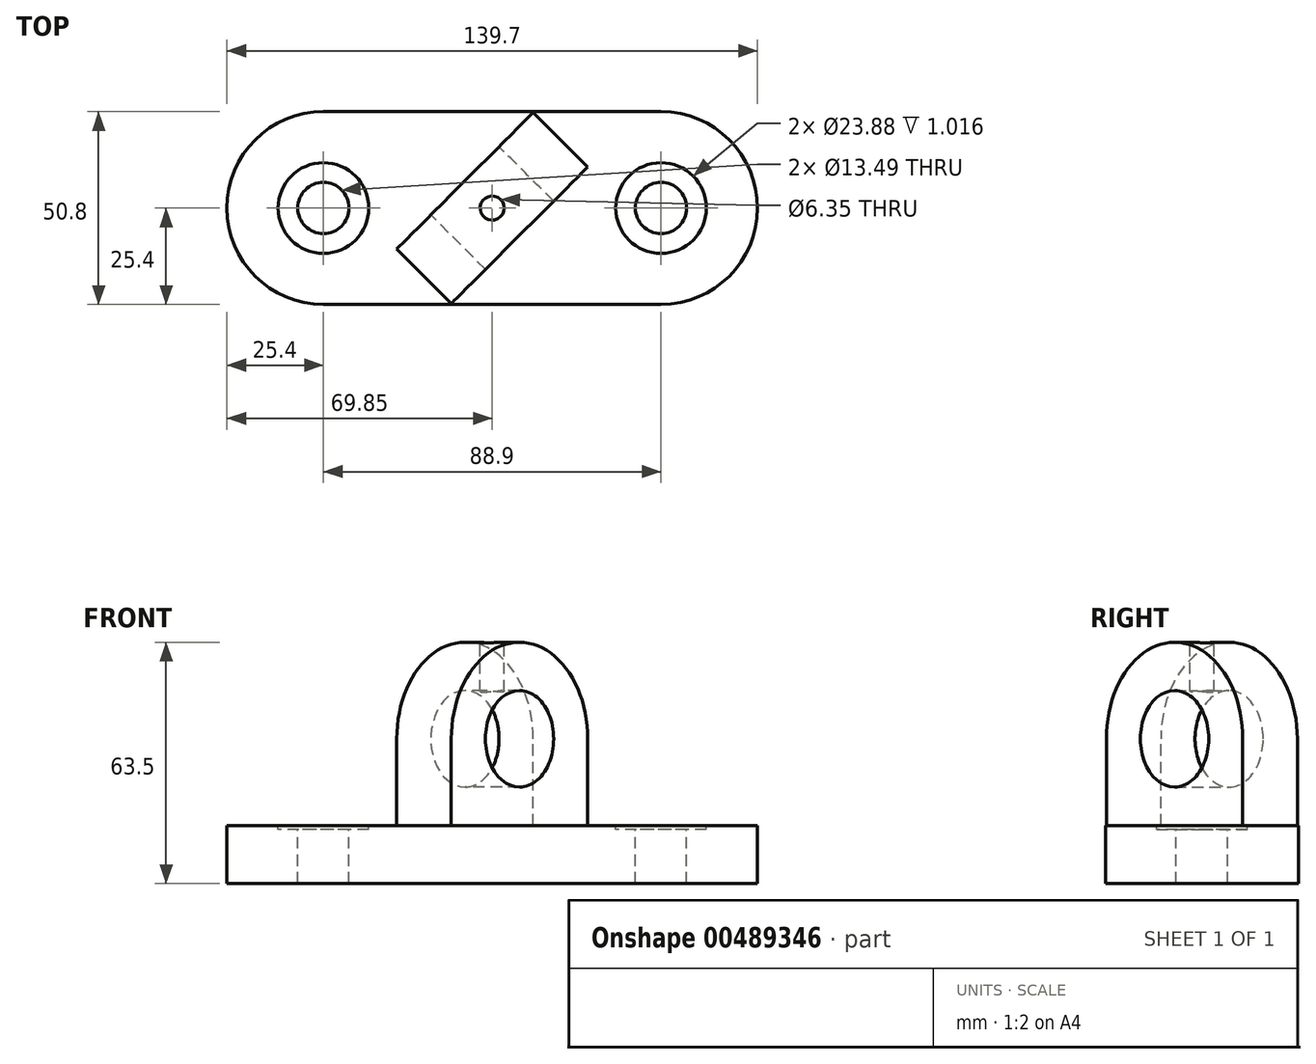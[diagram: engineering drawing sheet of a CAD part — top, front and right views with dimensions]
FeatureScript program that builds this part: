
annotation { "Feature Type Name" : "Feature", "Feature Type Description" : "" }
export const myFeature = defineFeature(function(context is Context, id is Id, definition is map)
    precondition{}
    {
        {
            var Q0;
            Q0=qCreatedBy(makeId("Top.planeOp"),FACE);
            var sketch = newSketch(context, id + "F0", { "sketchPlane" : qUnion([Q0])});
            skLineSegment(sketch, "E0.bottom", {"start": v(44.45, -25.4) * mm, "end": v(-44.45, -25.4) * mm});
            skLineSegment(sketch, "E0.top", {"start": v(44.45, 25.4) * mm, "end": v(-44.45, 25.4) * mm});
            skLineSegment(sketch, "E0.left", {"start": v(44.45, -25.4) * mm, "end": v(44.45, 25.4) * mm});
            skLineSegment(sketch, "E0.right", {"start": v(-44.45, -25.4) * mm, "end": v(-44.45, 25.4) * mm});
            skPoint(sketch, "E0.middle", {"position": v(0, 0) * mm});
            skCircle(sketch, "E1", {"center": v(-44.45, 0) * mm, "radius": 25.4 * mm});
            skCircle(sketch, "E2", {"center": v(44.45, 0) * mm, "radius": 25.4 * mm});
            skSolve(sketch);
        }
        {
            var Q0;
            Q0=qSketchRegion(id+"F0",true);
            extrude(context, id + "F1", {"entities" : qUnion([Q0]), "depth" : 15.24 * mm});
        }
        {
            var Q0;
            Q0=makeQuery(id+"F1.opExtrude","CAP_FACE",FACE,{"disambiguationData":[OSD([sQuery(id+"F0.wireOp",EDGE,"E0.bottom"),sQuery(id+"F0.wireOp",EDGE,"E0.top"),sQuery(id+"F0.wireOp",EDGE,"E1"),sQuery(id+"F0.wireOp",EDGE,"E2")])],"isStart":false});
            var sketch = newSketch(context, id + "F2", { "sketchPlane" : qUnion([Q0])});
            skCircle(sketch, "E3", {"center": v(44.45, 0) * mm, "radius": 6.74 * mm});
            skCircle(sketch, "E4", {"center": v(-44.45, 0) * mm, "radius": 6.74 * mm});
            skCircle(sketch, "E5", {"center": v(-44.45, 0) * mm, "radius": 11.94 * mm});
            skCircle(sketch, "E6", {"center": v(44.45, 0) * mm, "radius": 11.94 * mm});
            skSolve(sketch);
        }
        {
            var Q0;
            Q0=makeQuery(id+"F2.imprint","IMPRINT",FACE,{"disambiguationData":[TD([[makeQuery(id+"F2.imprint","IMPRINT",EDGE,{"derivedFrom":sQuery(id+"F2.wireOp",EDGE,"E3")}),-1.0]])]});
            var Q1;
            Q1=makeQuery(id+"F2.imprint","IMPRINT",FACE,{"disambiguationData":[TD([[makeQuery(id+"F2.imprint","IMPRINT",EDGE,{"derivedFrom":sQuery(id+"F2.wireOp",EDGE,"E4")}),-1.0]])]});
            extrude(context, id + "F3", {"entities" : qUnion([Q0, Q1]), "operationType" : NewBodyOperationType.REMOVE, "oppositeDirection" : true, "depth" : 1.02 * mm});
        }
        {
            var Q0;
            Q0=makeQuery(id+"F2.imprint","IMPRINT",FACE,{"disambiguationData":[TD([[makeQuery(id+"F2.imprint","IMPRINT",EDGE,{"derivedFrom":sQuery(id+"F2.wireOp",EDGE,"E3")}),1.0]])]});
            var Q1;
            Q1=makeQuery(id+"F2.imprint","IMPRINT",FACE,{"disambiguationData":[TD([[makeQuery(id+"F2.imprint","IMPRINT",EDGE,{"derivedFrom":sQuery(id+"F2.wireOp",EDGE,"E4")}),1.0]])]});
            extrude(context, id + "F4", {"entities" : qUnion([Q0, Q1]), "operationType" : NewBodyOperationType.REMOVE, "endBound" : BoundingType.THROUGH_ALL, "oppositeDirection" : true, "depth" : 25.4 * mm});
        }
        {
            var Q0;
            Q0=qCreatedBy(makeId("Front.planeOp"),FACE);
            var sketch = newSketch(context, id + "F5", { "sketchPlane" : qUnion([Q0])});
            skLineSegment(sketch, "E7", {"start": v(0, 0) * mm, "end": v(0, 87.66) * mm, "construction": true});
            skSolve(sketch);
        }
        {
            var Q0;
            Q0=sQuery(id+"F5.wireOp",EDGE,"E7");
            cPlane(context, id + "F6", {"entities" : qUnion([Q0]), "cplaneType" : CPlaneType.LINE_ANGLE, "offset" : 25.4 * mm, "angle" : 315 * degree, "width" : 152.4 * mm, "height" : 152.4 * mm});
        }
        {
            var Q0;
            Q0=qCreatedBy(id+"F6.planeOp",FACE);
            var sketch = newSketch(context, id + "F7", { "sketchPlane" : qUnion([Q0])});
            skLineSegment(sketch, "E8.top", {"start": v(0, 63.5) * mm, "end": v(0, 63.5) * mm});
            skLineSegment(sketch, "E8.left", {"start": v(-25.4, 15.24) * mm, "end": v(-25.4, 38.1) * mm});
            skLineSegment(sketch, "E8.right", {"start": v(25.4, 15.24) * mm, "end": v(25.4, 38.1) * mm});
            skPoint(sketch, "E8.middle", {"position": v(0, 38.1) * mm});
            skCircle(sketch, "E9", {"center": v(0, 38.1) * mm, "radius": 12.7 * mm});
            skArc(sketch, "E10.filletArc", {"start": v(0, 63.5) * mm, "mid": v(-17.96, 56.06) * mm, "end": v(-25.4, 38.1) * mm});
            skArc(sketch, "E11.filletArc", {"start": v(25.4, 38.1) * mm, "mid": v(17.96, 56.06) * mm, "end": v(0, 63.5) * mm});
            skLineSegment(sketch, "E12.0", {"start": v(13.47, 15.24) * mm, "end": v(-49.4, 15.24) * mm, "construction": true});
            skLineSegment(sketch, "E13.0", {"start": v(13.47, 15.24) * mm, "end": v(56.83, 15.24) * mm, "construction": true});
            skLineSegment(sketch, "E14", {"start": v(-25.4, 15.24) * mm, "end": v(25.4, 15.24) * mm});
            skSolve(sketch);
        }
        {
            var Q0;
            Q0=qSketchRegion(id+"F7",true);
            extrude(context, id + "F8", {"entities" : qUnion([Q0]), "operationType" : NewBodyOperationType.ADD, "endBound" : BoundingType.SYMMETRIC, "depth" : 20.32 * mm});
        }
        {
            var Q0;
            {var subQ0=sQuery(id+"F0.wireOp",EDGE,"E1");var subQ1=sQuery(id+"F0.wireOp",EDGE,"E0.top");var subQ2=sQuery(id+"F0.wireOp",EDGE,"E2");var subQ3=sQuery(id+"F0.wireOp",EDGE,"E0.bottom");Q0=makeQuery(id+"F3.boolean.opBoolean","SPLIT",FACE,{"disambiguationData":[TD([makeQuery(id+"F1.opExtrude","SWEPT_FACE",FACE,{"disambiguationData":[OSD([subQ3])]})])],"derivedFrom":makeQuery(id+"F1.opExtrude","CAP_FACE",FACE,{"disambiguationData":[OSD([subQ3,subQ1,subQ0,subQ2])],"isStart":false})});}
            cPlane(context, id + "F9", {"entities" : qUnion([Q0]), "cplaneType" : CPlaneType.OFFSET, "offset" : 48.26 * mm, "width" : 152.4 * mm, "height" : 152.4 * mm});
        }
        {
            var Q0;
            Q0=qCreatedBy(id+"F9.planeOp",FACE);
            var sketch = newSketch(context, id + "F10", { "sketchPlane" : qUnion([Q0])});
            skCircle(sketch, "E15", {"center": v(0, 0) * mm, "radius": 3.18 * mm});
            skSolve(sketch);
        }
        {
            var Q0;
            Q0=makeQuery(id+"F10.imprint","IMPRINT",FACE,{"disambiguationData":[TD([[makeQuery(id+"F10.imprint","IMPRINT",EDGE,{"derivedFrom":sQuery(id+"F10.wireOp",EDGE,"E15")}),1.0]])]});
            extrude(context, id + "F11", {"entities" : qUnion([Q0]), "operationType" : NewBodyOperationType.REMOVE, "endBound" : BoundingType.UP_TO_NEXT, "oppositeDirection" : true, "depth" : 25.4 * mm});
        }
    });
